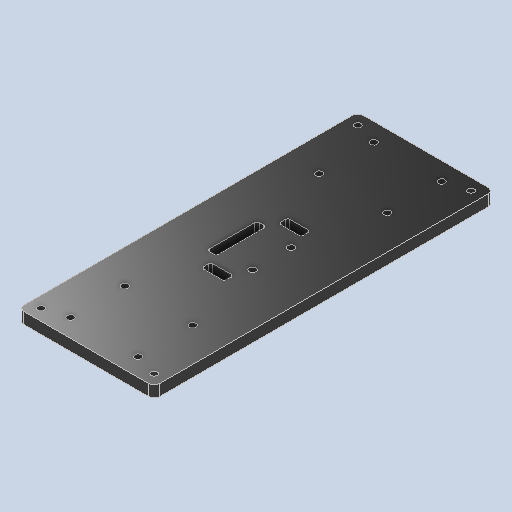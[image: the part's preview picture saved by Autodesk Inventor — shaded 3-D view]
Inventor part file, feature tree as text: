
AUTODESK INVENTOR PART (.ipt)
format: ipt  version: 2023 (Build 270158000, 158)  size: 182,784 bytes
history: native  units: in
note: dims shown in document units (in); Inventor stores cm internally (conversion verified against a paired STEP export)
features: other x3, sketch x1
ambient origin geometry x8: Origin, YZ Plane, XZ Plane, XY Plane, X Axis, Y Axis, Z Axis, Center Point
bodies: Solid1 (feature_tree)
feature tree (4):
  other  "DeDuoi.ipt"
  other  "Solid1::DeDuoi.ipt"
  other  "TaggingFeature1"
  sketch  "Sketch1"  dims[d0=0.3937in]
